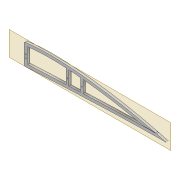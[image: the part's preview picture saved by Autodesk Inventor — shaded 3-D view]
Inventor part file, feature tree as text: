
AUTODESK INVENTOR PART (.ipt)
format: ipt  version: 2022 (Build 260153000, 153)  size: 352,256 bytes
history: native  units: mm
features: extrude x6, sketch x5, projected_geometry x4, shell x1, fillet x1, plane x1
ambient origin geometry x8: Origin, YZ Plane, XZ Plane, XY Plane, X Axis, Y Axis, Z Axis, Center Point
bodies: Solid1 (feature_tree)
feature tree (18):
  extrude  "Extrusion1"  Depth=5.0mm
  shell  "Shell1"  Thickness=6.0mm
  extrude  "Extrusion2"  Depth=2.0mm
  extrude  "Extrusion3"  Depth=5.9mm
  extrude  "Extrusion4"  Depth=10.0mm TaperAngle=0.0deg
  fillet  "Fillet1"  Radius=65.0mm
  extrude  "Extrusion5"  Depth=0.5mm TaperAngle=0.0deg
  plane  "Work Plane2"
  extrude  "Extrusion8"  Depth=0.5mm
  sketch  "Sketch3"  dims[d0=4.0mm d1=0.0mm d2=5.0mm d3=6.0mm]
  projected_geometry  "Projected Loop3"
  sketch  "Sketch8"  dims[d5=4.0mm d6=0.0mm d7=2.0mm]
  sketch  "Sketch9"  dims[d8=2.0mm d9=5.9mm]
  sketch  "Sketch10"  dims[d12=8.0mm d13=10.0mm d14=0.0mm d15=65.0mm]
  projected_geometry  "Projected Loop4"
  projected_geometry  "Projected Loop10"
  sketch  "Sketch16"  dims[d16=10.0mm d17=0.0mm d22=4.0mm d23=0.0mm d24=2.0mm d26=2.0mm d31=2.0mm d32=5.0mm d34=1.6mm d35=2.5mm d37=5.0mm d38=1.6mm d40=2.5mm d41=70.0mm d42=20.0mm d43=0.5mm d44=10.0mm d45=0.0mm]
  projected_geometry  "Projected Loop11"
